# Revit family: Haworth_Janus_Quinta_Stools
name_source: partatom
category: Furniture
revit_build: Autodesk Revit 2018 (Build: 20170223_1515(x64)
units: mm (PartAtom-declared; Revit-internal decimal feet)

## family parameters
Always vertical = Yes
Cut with Voids When Loaded = No
OmniClass Number = 23.40.70.14.64.21
OmniClass Title = Systems Furniture
Room Calculation Point = No
Shared = No
Work Plane-Based = No

## types (8) — shared parameters
Actual Depth = 22"
Actual Width = 19 3/4"
Assembly Code = E2020200
Glide Finish = Haworth _ Polymer _ Black
Manufacturer = Haworth
Revision Number = 2
Size = Verify Final Dim. w/ Haworth
URL = http://www.haworth.com
URL - Product = https://www.haworth.com
Warranty = https://www.haworth.com

## per-type parameters (varying)
| type | Actual Height | Cushion | Cushion Offset | Description | High | Low | Model | Seat Height |
| HCJC-QN-S3N-J - High - Fiber Frame - With Cushion | 45 1/2" | Yes | 2 121/128" | Haworth Janus Quinta - Barstool | Yes | No | HCJC-QN-S3N-J | 29 1/2" |
| HCJC-QN-S2N-J - Low - Fiber Frame - With Cushion | 42" | Yes | -3/8" | Haworth Janus Quinta - Counter Stool | No | Yes | HCJC-QN-S2N-J | 26" |
| HCJC-QN-S3N-J - High - Fiber Frame - No Cushion | 45 1/2" | No | 2 121/128" | Haworth Janus Quinta - Barstool | Yes | No | HCJC-QN-S3N-J | 29 1/2" |
| HCJC-QN-S2N-J - Low - Fiber Frame - No Cushion | 42" | No | -3/8" | Haworth Janus Quinta - Counter Stool | No | Yes | HCJC-QN-S2N-J | 26" |
| HCJC-QN-S2N-W - Low - Wood Frame - No Cushion | 42" | No | -3/8" | Haworth Janus Quinta - Counter Stool | No | Yes | HCJC-QN-S2N-W | 26" |
| HCJC-QN-S2N-W - Low - Wood Frame - With Cushion | 42" | Yes | -3/8" | Haworth Janus Quinta - Counter Stool | No | Yes | HCJC-QN-S2N-W | 26" |
| HCJC-QN-S3N-W - High - Wood Frame - No Cushion | 45 1/2" | No | 2 121/128" | Haworth Janus Quinta - Barstool | Yes | No | HCJC-QN-S3N-W | 29 1/2" |
| HCJC-QN-S3N-W - High - Wood Frame - With Cushion | 45 1/2" | Yes | 2 121/128" | Haworth Janus Quinta - Barstool | Yes | No | HCJC-QN-S3N-W | 29 1/2" |

## geometry (parser evidence)
native form markers: Sweep x5
no freeform markers — native parametric forms only
